# Revit family: RN 26005 Rubinetto a sfera
name_source: partatom
category: Rohrzubehör
units: mm (PartAtom-declared; Revit-internal decimal feet)

## family parameters
Arbeitsebenenbasiert = Nein
Beim Laden mit Abzugskörper schneiden = Nein
Bemaßung runder Anschluss = Durchmesser verwenden
Gemeinsam genutzt = Nein
Immer vertikal = Ja
Teiletyp = Ventil - Zerlegung in

## types (6) — shared parameters
1.010.00.2 Number of the part of the guideline = 2
1.010.00.3 Issue date (month) of the guideline = 201601
1.010.00.4 Manufacturer name = R. Nussbaum AG
1.010.00.5 Revision date of the file = 20190514
1.100.00.3 Sort number for display sequence = 4
1.100.00.4 Product designation = Absperr- und Regelarmaturen
1.960/3L.00.8 Link (URL) = https://www.nussbaum.ch
2.700.00.4 valve assembly type = 11
2.700.00.7 maximum operating temperature TB [°C] = 100
2.700.00.8 maximum operating pressure(working pressure) ps [1.0 · 102 Pa] = 16
Connector Visibility = Nein
EnclosingSpace Visibility = Nein
Hersteller = R. Nussbauzm AG
Modell = 0
URL = https://www.nussbaum.ch

## per-type parameters (varying)
| type | 1.800.00.3 BS number | 1.810.00.3 Manufacturer’s reference number | 1.810.00.4 DATANORM number | 1.810.00.6 GTIN number | 2.700.00.26 product description | 2.700.00.5 nominal size DN | 2.700.00.6 kvs-value [m3/h] | CONNECTOR0_DIAMETER_dX_0r | CONNECTOR0_dX_00 | CONNECTOR0_dX_01 | CONNECTOR0_ref_dX | CONNECTOR1_DIAMETER_dX_0r | CONNECTOR1_dX_00 | CONNECTOR1_dX_01 | CONNECTOR1_ref_dX | R. Nussbaum AG 26005.54 en Visibility | R. Nussbaum AG 26005.55 en Visibility | R. Nussbaum AG 26005.56 en Visibility | R. Nussbaum AG 26005.57 en Visibility | R. Nussbaum AG 26005.58 en Visibility | R. Nussbaum AG 26005.59 en Visibility | Typenkommentare |
| DN 15 | 0040050000000000000000000000010010000000000000000100000000 | 26005.54 | 26005.54 | 7612945703262 | 26005.54, Kugelhahn, mit Aussengewinde, DN=15, R=½ | 15 | 35 | 15 mm | 34 mm | 20 mm | 34 mm | 15 mm | 21 mm | 34 mm | 34 mm | Ja | Nein | Nein | Nein | Nein | Nein | Valvola d'arrestoDN 15 |
| DN 20 | 0040050000000000000000000000010010000000000000000200000000 | 26005.55 | 26005.55 | 7612945703279 | 26005.55, Kugelhahn, mit Aussengewinde, DN=20, R=¾ | 20 | 47 | 20 mm | 38 mm  [stored 0.124672 ft] | 23 mm | 38 mm  [stored 0.124672 ft] | 20 mm | 24 mm | 39 mm  [stored 0.127953 ft] | 39 mm  [stored 0.127953 ft] | Nein | Ja | Nein | Nein | Nein | Nein | Valvola d'arrestoDN 20 |
| DN 25 | 0040050000000000000000000000010010000000000000000300000000 | 26005.56 | 26005.56 | 7612945703286 | 26005.56, Kugelhahn, mit Aussengewinde, DN=25, R=1 | 25 | 54 | 25 mm  [stored 0.082021 ft] | 46 mm  [stored 0.150919 ft] | 28 mm | 46 mm  [stored 0.150919 ft] | 25 mm  [stored 0.082021 ft] | 28 mm | 46 mm  [stored 0.150919 ft] | 46 mm  [stored 0.150919 ft] | Nein | Nein | Ja | Nein | Nein | Nein | Valvola d'arrestoDN 25 |
| DN 32 | 0040050000000000000000000000010010000000000000000400000000 | 26005.57 | 26005.57 | 7612945703293 | 26005.57, Kugelhahn, mit Aussengewinde, DN=32, R=1¼ | 32 | 82 | 32 mm | 51 mm | 33 mm | 51 mm | 32 mm | 33 mm | 51 mm | 51 mm | Nein | Nein | Nein | Ja | Nein | Nein | Valvola d'arrestoDN 32 |
| DN 40 | 0040050000000000000000000000010010000000000000000500000000 | 26005.58 | 26005.58 | 7612945703309 | 26005.58, Kugelhahn, mit Aussengewinde, DN=40, R=1½ | 40 | 160 | 40 mm | 59 mm | 37 mm | 59 mm | 40 mm | 39 mm  [stored 0.127953 ft] | 58 mm | 58 mm | Nein | Nein | Nein | Nein | Ja | Nein | Valvola d'arrestoDN 40 |
| DN 50 | 0040050000000000000000000000010010000000000000000600000000 | 26005.59 | 26005.59 | 7612945703316 | 26005.59, Kugelhahn, mit Aussengewinde, DN=50, R=2 | 50 | 230 | 50 mm  [stored 0.164042 ft] | 69 mm | 43 mm  [stored 0.141076 ft] | 69 mm | 50 mm  [stored 0.164042 ft] | 43 mm  [stored 0.141076 ft] | 68 mm | 68 mm | Nein | Nein | Nein | Nein | Nein | Ja | Valvola d'arrestoDN 50 |

note: [stored X ft] marks values corroborated as IEEE doubles in the binary element streams (Revit-internal decimal feet)
